# Revit family: Haworth_Epure_CompactDesk_Asymmetrical120_EU_PRELIMINARY
name_source: partatom
category: Furniture
units: mm (PartAtom-declared; Revit-internal decimal feet)

## family parameters
Always vertical = Yes
Cut with Voids When Loaded = No
OmniClass Number = 23.40.70.14.64.11
OmniClass Title = Office Furniture
Room Calculation Point = No
Shared = No
Work Plane-Based = No

## types (2) — shared parameters
Actual Depth = 80 cm
Actual Height = 73 cm
Actual Width = 140 cm
Assembly Code = E2020200
Description = Haworth - Epure - Asymmetrical Compact Desk
Flip Top Finish = Haworth _ Paint _ Metallic Silver
Leg Height = 70 cm
Manufacturer = Haworth
Model = EUCO121408
Revision Number = 1
Size = Verify Final Dim.w/ Haworth
Trim Finish = Haworth _ Metal _ Structured White EC
URL = https://www.haworth.com
URL - Product = https://www.haworth.com
Warranty = http://www.haworth.com

## per-type parameters (varying)
| type | Accessory Kit | Cable Outlet | Flip Top Cable Outlet | No Accessory Kit | Rounded Corners | Squared Corners |
| 140w x 120deg - squared | Yes | Yes | Yes | No | No | Yes |
| 140w x 120deg - rounded | No | No | No | Yes | Yes | No |

type visibility flags: 2 boolean params named "<type name>" — each type sets only its own to Yes (folded from table)

## geometry (parser evidence)
native form markers: Sweep x14
no freeform markers — native parametric forms only
